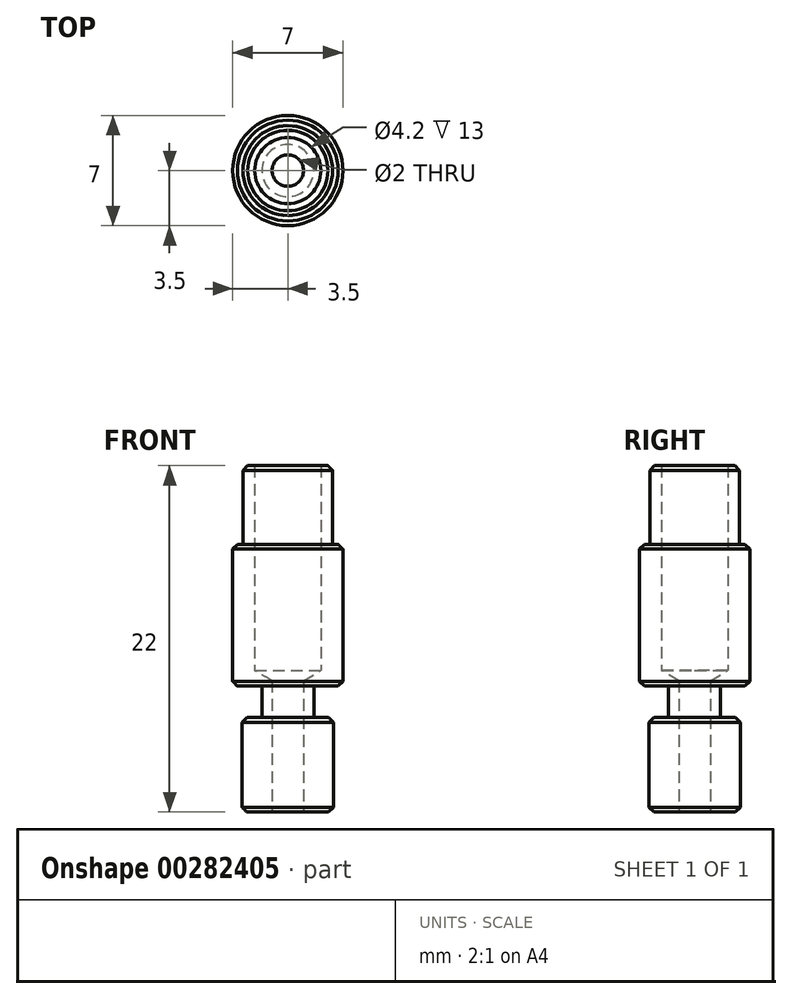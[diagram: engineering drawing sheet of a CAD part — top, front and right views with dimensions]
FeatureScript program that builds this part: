
annotation { "Feature Type Name" : "Feature", "Feature Type Description" : "" }
export const myFeature = defineFeature(function(context is Context, id is Id, definition is map)
    precondition{}
    {
        {
            var Q0;
            Q0=qCreatedBy(makeId("Front.planeOp"),FACE);
            var sketch = newSketch(context, id + "F0", { "sketchPlane" : qUnion([Q0])});
            skLineSegment(sketch, "E0", {"start": v(0, 0) * mm, "end": v(0, 22) * mm, "construction": true});
            skLineSegment(sketch, "E1", {"start": v(2.1, 22) * mm, "end": v(2.1, 9) * mm});
            skLineSegment(sketch, "E2", {"start": v(2.1, 9) * mm, "end": v(1, 8.34) * mm});
            skLineSegment(sketch, "E3", {"start": v(1, 8.34) * mm, "end": v(1, 0) * mm});
            skLineSegment(sketch, "E4", {"start": v(1, 0) * mm, "end": v(2.9, 0) * mm});
            skLineSegment(sketch, "E5", {"start": v(2.9, 0) * mm, "end": v(2.9, 6) * mm});
            skLineSegment(sketch, "E6", {"start": v(2.9, 6) * mm, "end": v(1.65, 6) * mm});
            skLineSegment(sketch, "E7", {"start": v(1.65, 6) * mm, "end": v(1.65, 8) * mm});
            skLineSegment(sketch, "E8", {"start": v(1.65, 8) * mm, "end": v(3.5, 8) * mm});
            skLineSegment(sketch, "E9", {"start": v(3.5, 8) * mm, "end": v(3.5, 17) * mm});
            skLineSegment(sketch, "E10", {"start": v(3.5, 17) * mm, "end": v(2.85, 17) * mm});
            skLineSegment(sketch, "E11", {"start": v(2.85, 17) * mm, "end": v(2.85, 22) * mm});
            skLineSegment(sketch, "E12", {"start": v(2.85, 22) * mm, "end": v(2.1, 22) * mm});
            skSolve(sketch);
        }
        {
            var Q0;
            Q0=qSketchRegion(id+"F0",true);
            var Q1;
            Q1=sQuery(id+"F0.wireOp",EDGE,"E0");
            revolve(context, id + "F1", {"entities" : qUnion([Q0]), "axis" : qUnion([Q1]), "revolveType" : RevolveType.FULL});
        }
        {
            var Q0;
            Q0=makeQuery(id+"F1.opRevolve","SWEPT_EDGE",EDGE,{"disambiguationData":[OSD([sQuery(id+"F0.wireOp",EDGE,"E11"),sQuery(id+"F0.wireOp",EDGE,"E12")])]});
            var Q1;
            Q1=makeQuery(id+"F1.opRevolve","SWEPT_EDGE",EDGE,{"disambiguationData":[OSD([sQuery(id+"F0.wireOp",EDGE,"E9"),sQuery(id+"F0.wireOp",EDGE,"E10")])]});
            var Q2;
            Q2=makeQuery(id+"F1.opRevolve","SWEPT_EDGE",EDGE,{"disambiguationData":[OSD([sQuery(id+"F0.wireOp",EDGE,"E8"),sQuery(id+"F0.wireOp",EDGE,"E9")])]});
            var Q3;
            Q3=makeQuery(id+"F1.opRevolve","SWEPT_EDGE",EDGE,{"disambiguationData":[OSD([sQuery(id+"F0.wireOp",EDGE,"E5"),sQuery(id+"F0.wireOp",EDGE,"E6")])]});
            var Q4;
            Q4=makeQuery(id+"F1.opRevolve","SWEPT_EDGE",EDGE,{"disambiguationData":[OSD([sQuery(id+"F0.wireOp",EDGE,"E4"),sQuery(id+"F0.wireOp",EDGE,"E5")])]});
            chamfer(context, id + "F2", {"entities" : qUnion([Q0, Q1, Q2, Q3, Q4]), "width" : 0.3 * mm, "tangentPropagation" : true});
        }
    });
